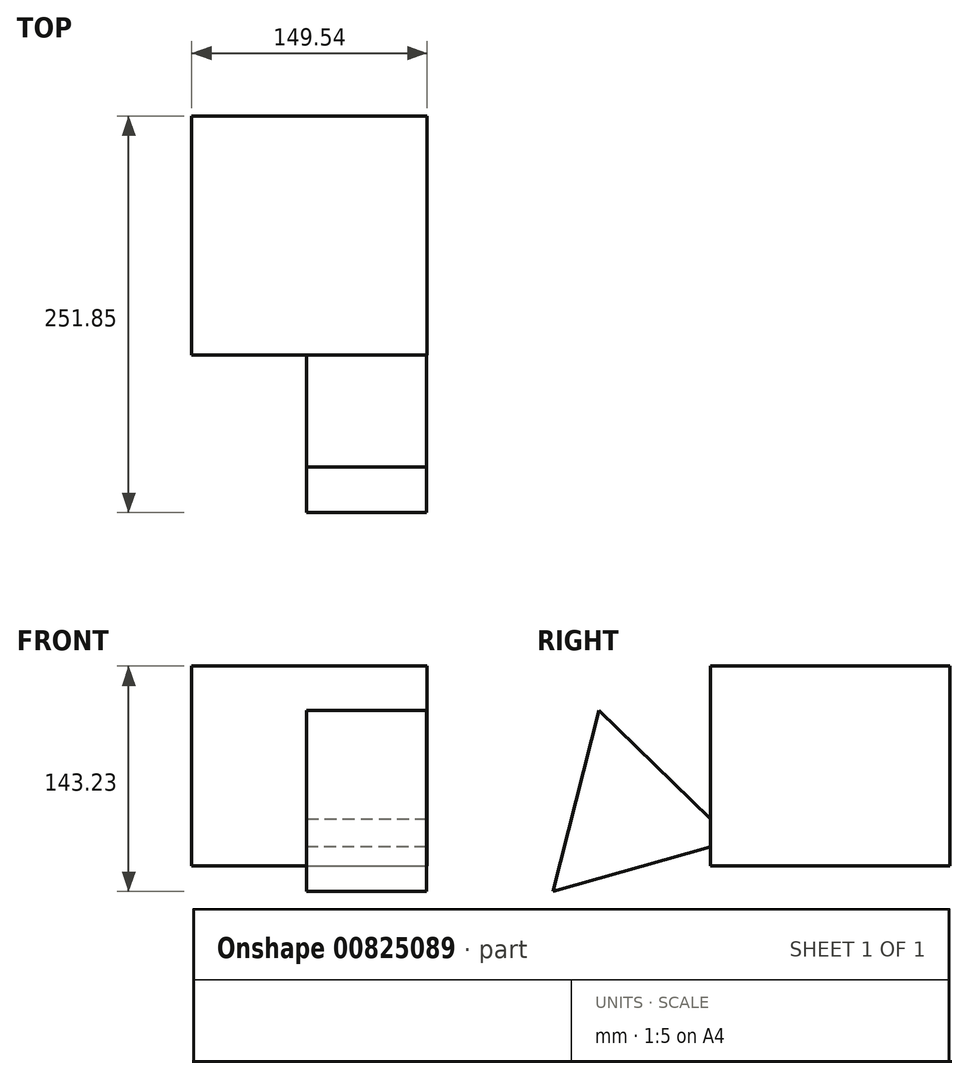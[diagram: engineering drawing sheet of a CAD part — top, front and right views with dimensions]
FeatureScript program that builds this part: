
annotation { "Feature Type Name" : "Feature", "Feature Type Description" : "" }
export const myFeature = defineFeature(function(context is Context, id is Id, definition is map)
    precondition{}
    {
        {
            var Q0;
            Q0=qCreatedBy(makeId("Top.planeOp"),FACE);
            var sketch = newSketch(context, id + "F0", { "sketchPlane" : qUnion([Q0])});
            skLineSegment(sketch, "E0.bottom", {"start": v(-72.93, 75.9) * mm, "end": v(76.61, 75.9) * mm});
            skLineSegment(sketch, "E0.top", {"start": v(-72.93, -75.9) * mm, "end": v(76.61, -75.9) * mm});
            skLineSegment(sketch, "E0.left", {"start": v(-72.93, 75.9) * mm, "end": v(-72.93, -75.9) * mm});
            skLineSegment(sketch, "E0.right", {"start": v(76.61, 75.9) * mm, "end": v(76.61, -75.9) * mm});
            skSolve(sketch);
        }
        {
            var Q0;
            Q0=makeQuery(id+"F0.imprint","IMPRINT",FACE,{"disambiguationData":[TD([[makeQuery(id+"F0.imprint","IMPRINT",EDGE,{"derivedFrom":sQuery(id+"F0.wireOp",EDGE,"E0.bottom")}),-1.0]])]});
            extrude(context, id + "F1", {"entities" : qUnion([Q0]), "depth" : 127 * mm, "offsetDistance" : 25.4 * mm});
        }
        {
            var Q0;
            Q0=qCreatedBy(makeId("Right.planeOp"),FACE);
            var sketch = newSketch(context, id + "F2", { "sketchPlane" : qUnion([Q0])});
            skCircle(sketch, "E1.cCircle", {"center": v(-128.25, 32.95) * mm, "radius": 34.26 * mm, "construction": true});
            skLineSegment(sketch, "E1.0", {"start": v(-61.8, 16.23) * mm, "end": v(-175.95, -16.23) * mm});
            skLineSegment(sketch, "E1.1", {"start": v(-175.95, -16.23) * mm, "end": v(-147, 98.85) * mm});
            skLineSegment(sketch, "E1.2", {"start": v(-147, 98.85) * mm, "end": v(-61.8, 16.23) * mm});
            skPoint(sketch, "E1.0.midPoint", {"position": v(-118.88, 0) * mm});
            skSolve(sketch);
        }
        {
            var Q0;
            Q0 = qSketchRegion(id + "F2", true);
            extrude(context, id + "F3", {"entities" : qUnion([Q0]), "operationType" : NewBodyOperationType.ADD, "depth" : 76.2 * mm, "offsetDistance" : 25.4 * mm});
        }
    });
